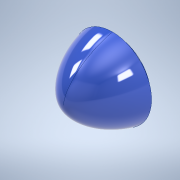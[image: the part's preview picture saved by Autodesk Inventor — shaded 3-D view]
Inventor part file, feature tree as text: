
AUTODESK INVENTOR PART (.ipt)
format: ipt  version: 2020 (Build 240168000, 168)  size: 278,016 bytes
history: native  units: mm
features: sketch x1, revolve x1
ambient origin geometry x8: Origin, YZ Plane, XZ Plane, XY Plane, X Axis, Y Axis, Z Axis, Center Point
bodies: Body1 (feature_tree)
feature tree (2):
  sketch  "Sketch1"  dims[d44=10.0mm d45=5.0mm d46=4.0mm d47=5.0mm d48=90.0deg d49=30.0mm d50=40.0mm d51=10.0mm d11=0.872665mm d12=0.872665mm]
  revolve  "Revolution3"  [1 undecoded]
note: 1 required parameter value undecoded (feature->parameter linkage not recoverable at this tier; creation-order binding heuristic only, values carry confidence <= 0.55)
